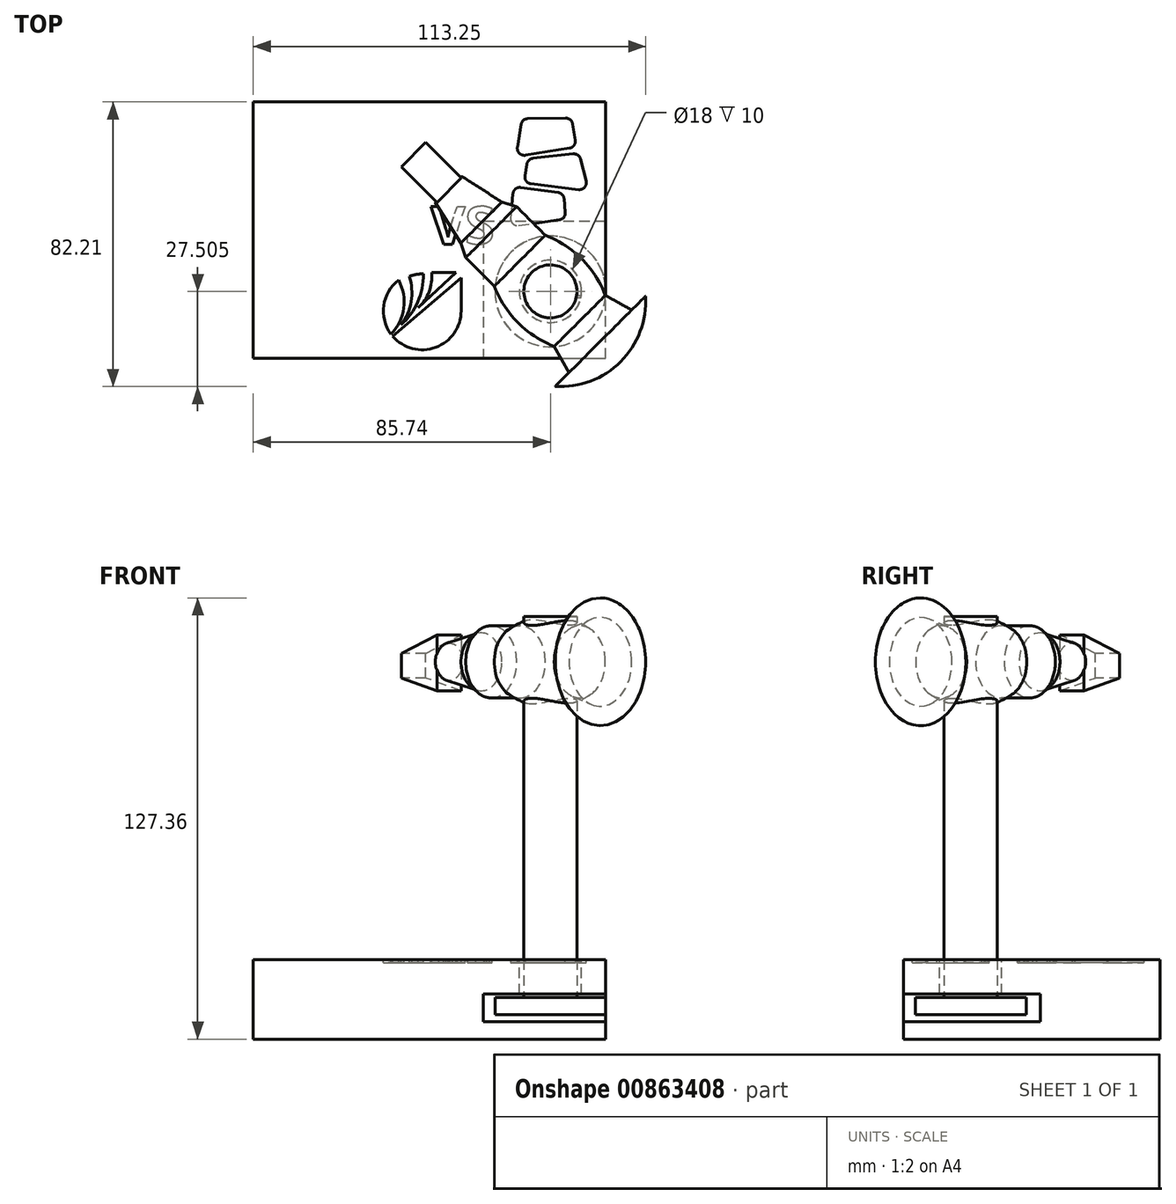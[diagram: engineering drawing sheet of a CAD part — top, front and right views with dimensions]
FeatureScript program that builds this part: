
annotation { "Feature Type Name" : "Feature", "Feature Type Description" : "" }
export const myFeature = defineFeature(function(context is Context, id is Id, definition is map)
    precondition{}
    {
        {
            var Q0;
            Q0=qCreatedBy(makeId("Top.planeOp"),FACE);
            cPlane(context, id + "F0", {"entities" : qUnion([Q0]), "cplaneType" : CPlaneType.OFFSET, "offset" : 36 * mm, "oppositeDirection" : true, "width" : 150 * mm, "height" : 150 * mm});
        }
        {
            var Q0;
            Q0=qCreatedBy(makeId("Top.planeOp"),FACE);
            cPlane(context, id + "F1", {"entities" : qUnion([Q0]), "cplaneType" : CPlaneType.OFFSET, "offset" : 40 * mm, "width" : 150 * mm, "height" : 150 * mm});
        }
        {
            var Q0;
            Q0=qCreatedBy(makeId("Front.planeOp"),FACE);
            var sketch = newSketch(context, id + "F2", { "sketchPlane" : qUnion([Q0])});
            skLineSegment(sketch, "E0", {"start": v(0, 86.74) * mm, "end": v(0, -86.44) * mm});
            skSolve(sketch);
        }
        {
            var Q0;
            Q0=sQuery(id+"F2.wireOp",EDGE,"E0");
            var Q1;
            Q1=qCreatedBy(makeId("Front.planeOp"),FACE);
            cPlane(context, id + "F3", {"entities" : qUnion([Q0, Q1]), "cplaneType" : CPlaneType.LINE_ANGLE, "offset" : 25 * mm, "angle" : 45 * degree, "width" : 150 * mm, "height" : 150 * mm});
        }
        {
            var Q0;
            Q0=qCreatedBy(id+"F3.planeOp",FACE);
            cPlane(context, id + "F4", {"entities" : qUnion([Q0]), "cplaneType" : CPlaneType.OFFSET, "offset" : 25 * mm, "width" : 150 * mm, "height" : 150 * mm});
        }
        {
            var Q0;
            Q0=qCreatedBy(id+"F4.planeOp",FACE);
            var sketch = newSketch(context, id + "F5", { "sketchPlane" : qUnion([Q0])});
            skLineSegment(sketch, "E1", {"start": v(-75.39, 49.92) * mm, "end": v(-11.92, 49.92) * mm});
            skLineSegment(sketch, "E2", {"start": v(-11.92, 49.92) * mm, "end": v(-11.92, 55.3) * mm});
            skLineSegment(sketch, "E3", {"start": v(-73.9, 62.7) * mm, "end": v(-73.9, 68.36) * mm});
            skLineSegment(sketch, "E4", {"start": v(-29.35, 60.33) * mm, "end": v(-41.03, 60.33) * mm});
            skArc(sketch, "E5", {"start": v(-41.03, 60.33) * mm, "mid": v(-53.27, 62.93) * mm, "end": v(-65.52, 60.33) * mm});
            skLineSegment(sketch, "E6", {"start": v(-65.52, 60.33) * mm, "end": v(-73.9, 62.7) * mm});
            skLineSegment(sketch, "E7", {"start": v(-11.92, 55.3) * mm, "end": v(-25.37, 58.26) * mm});
            skLineSegment(sketch, "E8", {"start": v(-25.37, 58.26) * mm, "end": v(-29.35, 60.33) * mm});
            skArc(sketch, "E9", {"start": v(-73.9, 68.36) * mm, "mid": v(-80.03, 60.03) * mm, "end": v(-82.2, 49.92) * mm});
            skLineSegment(sketch, "E10", {"start": v(-75.39, 49.92) * mm, "end": v(-82.2, 49.92) * mm});
            skSolve(sketch);
        }
        {
            var Q0;
            Q0=qSketchRegion(id+"F5",true);
            var Q1;
            Q1=sQuery(id+"F5.wireOp",EDGE,"E1");
            revolve(context, id + "F6", {"surfaceOperationType" : NewSurfaceOperationType.NEW, "entities" : qUnion([Q0]), "axis" : qUnion([Q1]), "revolveType" : RevolveType.FULL});
        }
        {
            var Q0;
            Q0=qCreatedBy(id+"F4.planeOp",FACE);
            var sketch = newSketch(context, id + "F7", { "sketchPlane" : qUnion([Q0])});
            skLineSegment(sketch, "E11", {"start": v(-12.2, 57.73) * mm, "end": v(-12.2, 41.5) * mm});
            skLineSegment(sketch, "E12", {"start": v(-12.2, 41.5) * mm, "end": v(2.33, 45.24) * mm});
            skLineSegment(sketch, "E13", {"start": v(2.33, 45.24) * mm, "end": v(2.33, 52.3) * mm});
            skLineSegment(sketch, "E14", {"start": v(2.33, 52.3) * mm, "end": v(-12.2, 57.73) * mm});
            skSolve(sketch);
        }
        {
            var Q0;
            Q0=qSketchRegion(id+"F7",true);
            extrude(context, id + "F8", {"entities" : qUnion([Q0]), "operationType" : NewBodyOperationType.ADD, "depth" : 5 * mm, "offsetDistance" : 25 * mm});
        }
        {
            var Q0;
            Q0=qSketchRegion(id+"F7",true);
            extrude(context, id + "F9", {"entities" : qUnion([Q0]), "operationType" : NewBodyOperationType.ADD, "oppositeDirection" : true, "depth" : 5 * mm, "offsetDistance" : 25 * mm});
        }
        {
            var Q0;
            Q0=qCreatedBy(id+"F0.planeOp",FACE);
            var sketch = newSketch(context, id + "F10", { "sketchPlane" : qUnion([Q0])});
            skCircle(sketch, "E15", {"center": v(55.51, -20.16) * mm, "radius": 7.65 * mm});
            skSolve(sketch);
        }
        {
            var Q0;
            Q0=qSketchRegion(id+"F10",true);
            extrude(context, id + "F11", {"entities" : qUnion([Q0]), "operationType" : NewBodyOperationType.ADD, "depth" : 99 * mm, "offsetDistance" : 25 * mm});
        }
        {
            var Q0;
            Q0=qCreatedBy(id+"F0.planeOp",FACE);
            var sketch = newSketch(context, id + "F12", { "sketchPlane" : qUnion([Q0])});
            skLineSegment(sketch, "E16.bottom", {"start": v(-30.23, -39.51) * mm, "end": v(71.47, -39.51) * mm});
            skLineSegment(sketch, "E16.top", {"start": v(-30.23, 34.55) * mm, "end": v(71.47, 34.55) * mm});
            skLineSegment(sketch, "E16.left", {"start": v(-30.23, -39.51) * mm, "end": v(-30.23, 34.55) * mm});
            skLineSegment(sketch, "E16.right", {"start": v(71.47, -39.51) * mm, "end": v(71.47, 34.55) * mm});
            skCircle(sketch, "E17", {"center": v(55.51, -20.16) * mm, "radius": 9 * mm});
            skSolve(sketch);
        }
        {
            var Q0;
            Q0=qSketchRegion(id+"F12",true);
            extrude(context, id + "F13", {"entities" : qUnion([Q0]), "operationType" : NewBodyOperationType.ADD, "oppositeDirection" : true, "depth" : 10 * mm, "offsetDistance" : 25 * mm});
        }
        {
            var Q0;
            Q0=qSketchRegion(id+"F10",true);
            extrude(context, id + "F14", {"entities" : qUnion([Q0]), "operationType" : NewBodyOperationType.ADD, "oppositeDirection" : true, "depth" : 15 * mm, "offsetDistance" : 25 * mm});
        }
        {
            var Q0;
            Q0=makeQuery(id+"F13.opExtrude","CAP_FACE",FACE,{"disambiguationData":[OSD([sQuery(id+"F12.wireOp",EDGE,"E16.bottom"),sQuery(id+"F12.wireOp",EDGE,"E16.top"),sQuery(id+"F12.wireOp",EDGE,"E16.left"),sQuery(id+"F12.wireOp",EDGE,"E16.right"),sQuery(id+"F12.wireOp",EDGE,"E17")])],"isStart":false});
            cPlane(context, id + "F15", {"entities" : qUnion([Q0]), "cplaneType" : CPlaneType.OFFSET, "offset" : 1 * mm, "width" : 150 * mm, "height" : 150 * mm});
        }
        {
            var Q0;
            Q0=qCreatedBy(id+"F15.planeOp",FACE);
            var sketch = newSketch(context, id + "F16", { "sketchPlane" : qUnion([Q0])});
            skCircle(sketch, "E18", {"center": v(55.51, 20.16) * mm, "radius": 16 * mm});
            skSolve(sketch);
        }
        {
            var Q0;
            Q0=qSketchRegion(id+"F16",true);
            extrude(context, id + "F17", {"entities" : qUnion([Q0]), "operationType" : NewBodyOperationType.ADD, "depth" : 5 * mm, "offsetDistance" : 25 * mm});
        }
        {
            var Q0;
            Q0=makeQuery(id+"F13.opExtrude","CAP_FACE",FACE,{"disambiguationData":[OSD([sQuery(id+"F12.wireOp",EDGE,"E16.bottom"),sQuery(id+"F12.wireOp",EDGE,"E16.top"),sQuery(id+"F12.wireOp",EDGE,"E16.left"),sQuery(id+"F12.wireOp",EDGE,"E16.right"),sQuery(id+"F12.wireOp",EDGE,"E17")])],"isStart":false});
            var sketch = newSketch(context, id + "F18", { "sketchPlane" : qUnion([Q0])});
            skLineSegment(sketch, "E19", {"start": v(71.47, -34.55) * mm, "end": v(71.47, 0) * mm});
            skLineSegment(sketch, "E20", {"start": v(71.47, 0) * mm, "end": v(36.17, 0) * mm});
            skLineSegment(sketch, "E21", {"start": v(-30.23, -34.55) * mm, "end": v(71.47, -34.55) * mm});
            skLineSegment(sketch, "E22", {"start": v(-30.23, -34.55) * mm, "end": v(-30.23, 0) * mm});
            skLineSegment(sketch, "E23", {"start": v(36.17, 0) * mm, "end": v(36.17, 39.51) * mm});
            skLineSegment(sketch, "E24", {"start": v(36.17, 39.51) * mm, "end": v(-30.23, 39.51) * mm});
            skLineSegment(sketch, "E25", {"start": v(-30.23, 39.51) * mm, "end": v(-30.23, 0) * mm});
            skSolve(sketch);
        }
        {
            var Q0;
            Q0=makeQuery(id+"F18.imprint","IMPRINT",FACE,{"disambiguationData":[TD([[makeQuery(id+"F18.imprint","IMPRINT",EDGE,{"derivedFrom":sQuery(id+"F18.wireOp",EDGE,"E19")}),-1.0]])]});
            extrude(context, id + "F19", {"entities" : qUnion([Q0]), "operationType" : NewBodyOperationType.ADD, "depth" : 8 * mm, "offsetDistance" : 25 * mm});
        }
        {
            var Q0;
            Q0=makeQuery(id+"F19.opExtrude","CAP_FACE",FACE,{"disambiguationData":[OSD([sQuery(id+"F18.wireOp",EDGE,"E19"),sQuery(id+"F18.wireOp",EDGE,"E20"),sQuery(id+"F18.wireOp",EDGE,"E21"),sQuery(id+"F18.wireOp",EDGE,"iN0juFn1-ICa9-M7KA-fJVA-QljqQybucplU"),sQuery(id+"F18.wireOp",EDGE,"E22")])],"isStart":false});
            var sketch = newSketch(context, id + "F20", { "sketchPlane" : qUnion([Q0])});
            skLineSegment(sketch, "E26.bottom", {"start": v(-30.23, -34.55) * mm, "end": v(71.47, -34.55) * mm});
            skLineSegment(sketch, "E26.top", {"start": v(-30.23, 39.51) * mm, "end": v(71.47, 39.51) * mm});
            skLineSegment(sketch, "E26.left", {"start": v(-30.23, -34.55) * mm, "end": v(-30.23, 39.51) * mm});
            skLineSegment(sketch, "E26.right", {"start": v(71.47, -34.55) * mm, "end": v(71.47, 39.51) * mm});
            skSolve(sketch);
        }
        {
            var Q0;
            Q0=qSketchRegion(id+"F20",true);
            extrude(context, id + "F21", {"entities" : qUnion([Q0]), "operationType" : NewBodyOperationType.ADD, "depth" : 5 * mm, "offsetDistance" : 25 * mm});
        }
        {
            var Q0;
            Q0=makeQuery(id+"F13.opExtrude","CAP_FACE",FACE,{"disambiguationData":[OSD([sQuery(id+"F12.wireOp",EDGE,"E16.bottom"),sQuery(id+"F12.wireOp",EDGE,"E16.top"),sQuery(id+"F12.wireOp",EDGE,"E16.left"),sQuery(id+"F12.wireOp",EDGE,"E16.right"),sQuery(id+"F12.wireOp",EDGE,"E17")])],"isStart":true});
            var sketch = newSketch(context, id + "F22", { "sketchPlane" : qUnion([Q0])});
            skLineSegment(sketch, "E27.bottom", {"start": v(65.5, -22.08) * mm, "end": v(62.22, -22.08) * mm});
            skLineSegment(sketch, "E27.top", {"start": v(65.5, -21.47) * mm, "end": v(62.22, -21.47) * mm});
            skLineSegment(sketch, "E27.left", {"start": v(65.5, -22.08) * mm, "end": v(65.5, -21.47) * mm});
            skLineSegment(sketch, "E27.right", {"start": v(62.22, -22.08) * mm, "end": v(62.22, -21.47) * mm});
            skSolve(sketch);
        }
        {
            var Q0;
            Q0=qSketchRegion(id+"F22",true);
            extrude(context, id + "F23", {"entities" : qUnion([Q0]), "operationType" : NewBodyOperationType.ADD, "oppositeDirection" : true, "depth" : 0.5 * mm, "offsetDistance" : 25 * mm});
        }
        {
            var Q0;
            Q0=makeQuery(id+"F23.boolean.opBoolean","MERGE",FACE,{"derivedFrom":[makeQuery(id+"F13.opExtrude","CAP_FACE",FACE,{"disambiguationData":[OSD([sQuery(id+"F12.wireOp",EDGE,"E16.bottom"),sQuery(id+"F12.wireOp",EDGE,"E16.top"),sQuery(id+"F12.wireOp",EDGE,"E16.left"),sQuery(id+"F12.wireOp",EDGE,"E16.right"),sQuery(id+"F12.wireOp",EDGE,"E17")])],"isStart":true}),makeQuery(id+"F23.opExtrude","CAP_FACE",FACE,{"disambiguationData":[OSD([sQuery(id+"F22.wireOp",EDGE,"E27.bottom"),sQuery(id+"F22.wireOp",EDGE,"E27.top"),sQuery(id+"F22.wireOp",EDGE,"E27.left"),sQuery(id+"F22.wireOp",EDGE,"E27.right")])],"isStart":true})]});
            var sketch = newSketch(context, id + "F24", { "sketchPlane" : qUnion([Q0])});
            skLineSegment(sketch, "E28", {"start": v(47.35, 29.69) * mm, "end": v(45.56, 18.71) * mm});
            skLineSegment(sketch, "E29", {"start": v(45.56, 18.71) * mm, "end": v(63, 21.5) * mm});
            skLineSegment(sketch, "E30", {"start": v(63, 21.5) * mm, "end": v(61.68, 29.86) * mm});
            skLineSegment(sketch, "E31", {"start": v(61.68, 29.86) * mm, "end": v(47.35, 29.69) * mm});
            skLineSegment(sketch, "E32", {"start": v(48.97, 18.09) * mm, "end": v(47.85, 11.15) * mm});
            skLineSegment(sketch, "E33", {"start": v(47.85, 11.15) * mm, "end": v(66.52, 8.87) * mm});
            skLineSegment(sketch, "E34", {"start": v(63.83, 19.72) * mm, "end": v(48.97, 18.09) * mm});
            skLineSegment(sketch, "E35", {"start": v(63.83, 19.72) * mm, "end": v(66.52, 8.87) * mm});
            skLineSegment(sketch, "E36", {"start": v(44.9, 10.13) * mm, "end": v(43.84, -1.5) * mm});
            skLineSegment(sketch, "E37", {"start": v(43.84, -1.5) * mm, "end": v(59.99, 0.74) * mm});
            skLineSegment(sketch, "E38", {"start": v(59.3, 8.18) * mm, "end": v(44.9, 10.13) * mm});
            skLineSegment(sketch, "E39", {"start": v(59.3, 8.18) * mm, "end": v(59.99, 0.74) * mm});
            skSolve(sketch);
        }
        {
            var Q0;
            Q0=qSketchRegion(id+"F24",true);
            extrude(context, id + "F25", {"entities" : qUnion([Q0]), "operationType" : NewBodyOperationType.REMOVE, "oppositeDirection" : true, "depth" : 1 * mm, "offsetDistance" : 25 * mm});
        }
        {
            var Q0;
            Q0=makeQuery(id+"F25.boolean.opBoolean","COPY",EDGE,{"derivedFrom":makeQuery(id+"F25.opExtrude","SWEPT_EDGE",EDGE,{"disambiguationData":[OSD([sQuery(id+"F24.wireOp",EDGE,"E37"),sQuery(id+"F24.wireOp",EDGE,"E39")])]})});
            var Q1;
            Q1=makeQuery(id+"F25.boolean.opBoolean","COPY",EDGE,{"derivedFrom":makeQuery(id+"F25.opExtrude","SWEPT_EDGE",EDGE,{"disambiguationData":[OSD([sQuery(id+"F24.wireOp",EDGE,"E38"),sQuery(id+"F24.wireOp",EDGE,"E39")])]})});
            var Q2;
            Q2=makeQuery(id+"F25.boolean.opBoolean","COPY",EDGE,{"derivedFrom":makeQuery(id+"F25.opExtrude","SWEPT_EDGE",EDGE,{"disambiguationData":[OSD([sQuery(id+"F24.wireOp",EDGE,"E36"),sQuery(id+"F24.wireOp",EDGE,"E37")])]})});
            var Q3;
            Q3=makeQuery(id+"F25.boolean.opBoolean","COPY",EDGE,{"derivedFrom":makeQuery(id+"F25.opExtrude","SWEPT_EDGE",EDGE,{"disambiguationData":[OSD([sQuery(id+"F24.wireOp",EDGE,"E36"),sQuery(id+"F24.wireOp",EDGE,"E38")])]})});
            var Q4;
            Q4=makeQuery(id+"F25.boolean.opBoolean","COPY",EDGE,{"derivedFrom":makeQuery(id+"F25.opExtrude","SWEPT_EDGE",EDGE,{"disambiguationData":[OSD([sQuery(id+"F24.wireOp",EDGE,"E32"),sQuery(id+"F24.wireOp",EDGE,"E33")])]})});
            var Q5;
            Q5=makeQuery(id+"F25.boolean.opBoolean","COPY",EDGE,{"derivedFrom":makeQuery(id+"F25.opExtrude","SWEPT_EDGE",EDGE,{"disambiguationData":[OSD([sQuery(id+"F24.wireOp",EDGE,"E28"),sQuery(id+"F24.wireOp",EDGE,"E29")])]})});
            var Q6;
            Q6=makeQuery(id+"F25.boolean.opBoolean","COPY",EDGE,{"derivedFrom":makeQuery(id+"F25.opExtrude","SWEPT_EDGE",EDGE,{"disambiguationData":[OSD([sQuery(id+"F24.wireOp",EDGE,"E32"),sQuery(id+"F24.wireOp",EDGE,"E34")])]})});
            var Q7;
            Q7=makeQuery(id+"F25.boolean.opBoolean","COPY",EDGE,{"derivedFrom":makeQuery(id+"F25.opExtrude","SWEPT_EDGE",EDGE,{"disambiguationData":[OSD([sQuery(id+"F24.wireOp",EDGE,"E28"),sQuery(id+"F24.wireOp",EDGE,"E31")])]})});
            var Q8;
            Q8=makeQuery(id+"F25.boolean.opBoolean","COPY",EDGE,{"derivedFrom":makeQuery(id+"F25.opExtrude","SWEPT_EDGE",EDGE,{"disambiguationData":[OSD([sQuery(id+"F24.wireOp",EDGE,"E30"),sQuery(id+"F24.wireOp",EDGE,"E31")])]})});
            var Q9;
            Q9=makeQuery(id+"F25.boolean.opBoolean","COPY",EDGE,{"derivedFrom":makeQuery(id+"F25.opExtrude","SWEPT_EDGE",EDGE,{"disambiguationData":[OSD([sQuery(id+"F24.wireOp",EDGE,"E34"),sQuery(id+"F24.wireOp",EDGE,"E35")])]})});
            var Q10;
            Q10=makeQuery(id+"F25.boolean.opBoolean","COPY",EDGE,{"derivedFrom":makeQuery(id+"F25.opExtrude","SWEPT_EDGE",EDGE,{"disambiguationData":[OSD([sQuery(id+"F24.wireOp",EDGE,"E29"),sQuery(id+"F24.wireOp",EDGE,"E30")])]})});
            var Q11;
            Q11=makeQuery(id+"F25.boolean.opBoolean","COPY",EDGE,{"derivedFrom":makeQuery(id+"F25.opExtrude","SWEPT_EDGE",EDGE,{"disambiguationData":[OSD([sQuery(id+"F24.wireOp",EDGE,"E33"),sQuery(id+"F24.wireOp",EDGE,"E35")])]})});
            fillet(context, id + "F26", {"entities" : qUnion([Q0, Q1, Q2, Q3, Q4, Q5, Q6, Q7, Q8, Q9, Q10, Q11]), "radius" : 2 * mm, "tangentPropagation" : true, "allowEdgeOverflow" : false});
        }
        {
            var Q0;
            Q0=makeQuery(id+"F23.boolean.opBoolean","MERGE",FACE,{"derivedFrom":[makeQuery(id+"F13.opExtrude","CAP_FACE",FACE,{"disambiguationData":[OSD([sQuery(id+"F12.wireOp",EDGE,"E16.bottom"),sQuery(id+"F12.wireOp",EDGE,"E16.top"),sQuery(id+"F12.wireOp",EDGE,"E16.left"),sQuery(id+"F12.wireOp",EDGE,"E16.right"),sQuery(id+"F12.wireOp",EDGE,"E17")])],"isStart":true}),makeQuery(id+"F23.opExtrude","CAP_FACE",FACE,{"disambiguationData":[OSD([sQuery(id+"F22.wireOp",EDGE,"E27.bottom"),sQuery(id+"F22.wireOp",EDGE,"E27.top"),sQuery(id+"F22.wireOp",EDGE,"E27.left"),sQuery(id+"F22.wireOp",EDGE,"E27.right")])],"isStart":true})]});
            var sketch = newSketch(context, id + "F27", { "sketchPlane" : qUnion([Q0])});
            skArc(sketch, "E40", {"start": v(10.01, -33.1) * mm, "mid": v(22.42, -36.32) * mm, "end": v(29.75, -25.8) * mm});
            skLineSegment(sketch, "E41", {"start": v(29.75, -25.8) * mm, "end": v(29.75, -16.19) * mm});
            skLineSegment(sketch, "E42", {"start": v(29.75, -16.19) * mm, "end": v(18.53, -25.8) * mm});
            skLineSegment(sketch, "E43", {"start": v(10.01, -33.1) * mm, "end": v(18.53, -25.8) * mm});
            skLineSegment(sketch, "E44", {"start": v(28.26, -14.71) * mm, "end": v(21.29, -14.71) * mm});
            skLineSegment(sketch, "E45", {"start": v(28.26, -14.71) * mm, "end": v(17.39, -24.9) * mm});
            skArc(sketch, "E46", {"start": v(11.71, -16.9) * mm, "mid": v(7.42, -24.24) * mm, "end": v(9.53, -32.5) * mm});
            skArc(sketch, "E47", {"start": v(9.53, -32.5) * mm, "mid": v(13.18, -25.05) * mm, "end": v(11.71, -16.9) * mm});
            skArc(sketch, "E48", {"start": v(12.42, -29.83) * mm, "mid": v(15.32, -23.1) * mm, "end": v(14.8, -15.79) * mm});
            skArc(sketch, "E49", {"start": v(12.42, -29.83) * mm, "mid": v(17.27, -23.2) * mm, "end": v(18.83, -15.12) * mm});
            skArc(sketch, "E50", {"start": v(17.39, -24.9) * mm, "mid": v(20.5, -20.25) * mm, "end": v(21.29, -14.71) * mm});
            skArc(sketch, "E51", {"start": v(18.83, -15.12) * mm, "mid": v(16.78, -15.26) * mm, "end": v(14.8, -15.79) * mm});
            skText(sketch, "E52", { "text": "VS", "fontName": "OpenSans-Bold.ttf"});
            const initialGuessF27  = {"E52": [0.02102, -0.00654, 1, 0, 0.01097]};
            skSetInitialGuess(sketch, initialGuessF27);
            skSolve(sketch);
        }
        {
            var Q0;
            Q0=qSketchRegion(id+"F27",true);
            extrude(context, id + "F28", {"entities" : qUnion([Q0]), "operationType" : NewBodyOperationType.REMOVE, "oppositeDirection" : true, "depth" : 1 * mm, "offsetDistance" : 25 * mm});
        }
    });
